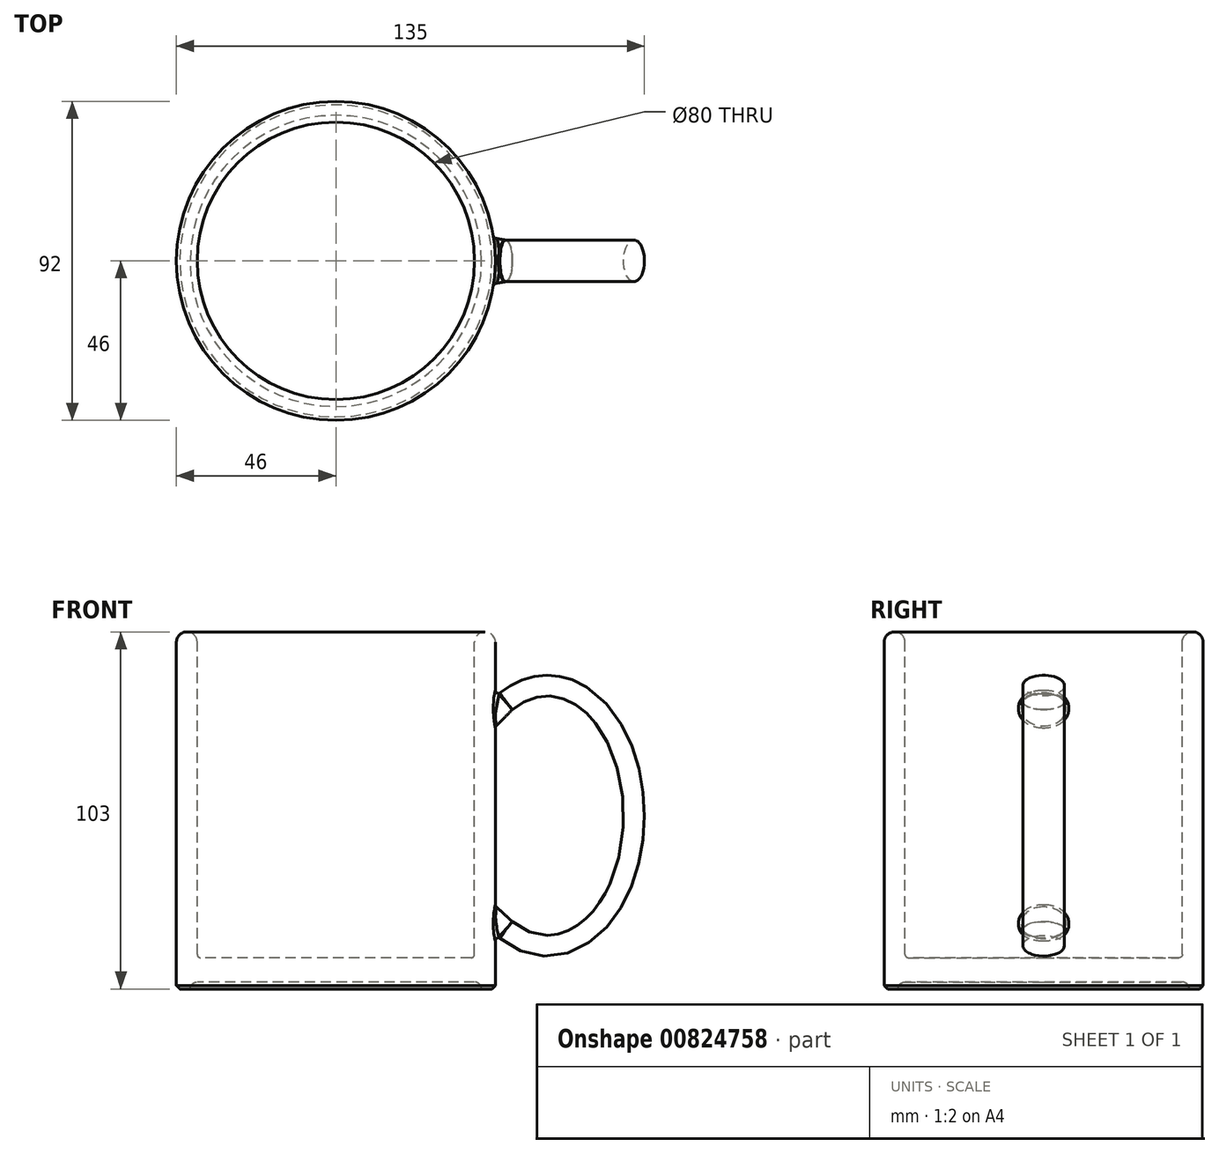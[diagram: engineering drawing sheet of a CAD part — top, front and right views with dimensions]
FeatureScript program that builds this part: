
annotation { "Feature Type Name" : "Feature", "Feature Type Description" : "" }
export const myFeature = defineFeature(function(context is Context, id is Id, definition is map)
    precondition{}
    {
        {
            var Q0;
            Q0=qCreatedBy(makeId("Front.planeOp"),FACE);
            var sketch = newSketch(context, id + "F0", { "sketchPlane" : qUnion([Q0])});
            skLineSegment(sketch, "E0", {"start": v(0, 1) * mm, "end": v(0, 91) * mm});
            skLineSegment(sketch, "E1", {"start": v(6, 91) * mm, "end": v(6, -9) * mm});
            skLineSegment(sketch, "E2", {"start": v(6, -9) * mm, "end": v(2, -9) * mm});
            skLineSegment(sketch, "E3", {"start": v(-1, 0) * mm, "end": v(-40, 0) * mm});
            skLineSegment(sketch, "E4", {"start": v(-40, 0) * mm, "end": v(-40, -7) * mm});
            skLineSegment(sketch, "E5", {"start": v(-40, -7) * mm, "end": v(0, -7) * mm});
            skLineSegment(sketch, "E6", {"start": v(2, -9) * mm, "end": v(2, -9) * mm});
            skArc(sketch, "E7", {"start": v(0, 91) * mm, "mid": v(3, 94) * mm, "end": v(6, 91) * mm});
            skPoint(sketch, "E8.visualSharp", {"position": v(2, -7) * mm});
            skArc(sketch, "E8.filletArc", {"start": v(2, -9) * mm, "mid": v(1.41, -7.59) * mm, "end": v(0, -7) * mm});
            skPoint(sketch, "E9.visualSharp", {"position": v(0, 0) * mm});
            skArc(sketch, "E9.filletArc", {"start": v(-1, 0) * mm, "mid": v(-0.3, 0.3) * mm, "end": v(0, 1) * mm});
            skLineSegment(sketch, "E10", {"start": v(6, 41) * mm, "end": v(21, 41) * mm, "construction": true});
            skEllipticalArc(sketch, "E11", {});
            skLineSegment(sketch, "E12", {"start": v(9, 87.43) * mm, "end": v(9, -6.06) * mm, "construction": true});
            const initialGuessF0  = {"E11": [0.021, 0.041, 0, 1, 0.0375, 0.025, 2.6409379411852054, 0.5006547124045883]};
            skSetInitialGuess(sketch, initialGuessF0);
            skSolve(sketch);
        }
        {
            var Q0;
            Q0=qCreatedBy(makeId("Right.planeOp"),FACE);
            var sketch = newSketch(context, id + "F1", { "sketchPlane" : qUnion([Q0])});
            skCircle(sketch, "E13", {"center": v(0, 68) * mm, "radius": 7.5 * mm});
            skCircle(sketch, "E14.0.1.0", {"center": v(0, 13) * mm, "radius": 7.5 * mm});
            skLineSegment(sketch, "E14.direction1", {"start": v(0, 68) * mm, "end": v(25, 68) * mm, "construction": true});
            skLineSegment(sketch, "E14.direction2", {"start": v(0, 68) * mm, "end": v(0, 13) * mm, "construction": true});
            skSolve(sketch);
        }
        {
            var Q0;
            Q0=qCreatedBy(makeId("Top.planeOp"),FACE);
            var Q1;
            Q1=sQuery(id+"F0.wireOp",VERTEX,"E10.end");
            cPlane(context, id + "F2", {"entities" : qUnion([Q0, Q1]), "cplaneType" : CPlaneType.PLANE_POINT, "offset" : 25 * mm, "width" : 150 * mm, "height" : 150 * mm});
        }
        {
            var Q0;
            Q0=qCreatedBy(id+"F2.planeOp",FACE);
            var sketch = newSketch(context, id + "F3", { "sketchPlane" : qUnion([Q0])});
            skLineSegment(sketch, "E15.0", {"start": v(9, 0) * mm, "end": v(46, 0) * mm, "construction": true});
            skEllipse(sketch, "E16", {"center": v(46, 0) * mm, "majorRadius": 6 * mm, "minorRadius": 3 * mm, "majorAxis": v(0, 1)});
            skSolve(sketch);
        }
        {
            var Q0;
            Q0=makeQuery(id+"F3.imprint","IMPRINT",FACE,{"disambiguationData":[TD([[makeQuery(id+"F3.imprint","IMPRINT",EDGE,{"derivedFrom":sQuery(id+"F3.wireOp",EDGE,"E16")}),1.0]])]});
            var Q1;
            Q1=sQuery(id+"F0.wireOp",EDGE,"E11");
            sweep(context, id + "F4", {"profiles" : qUnion([Q0]), "path" : qUnion([Q1])});
        }
        {
            var Q0;
            Q0=makeQuery(id+"F0.imprint","IMPRINT",FACE,{"disambiguationData":[TD([[makeQuery(id+"F0.imprint","IMPRINT",EDGE,{"derivedFrom":sQuery(id+"F0.wireOp",EDGE,"E0")}),-1.0]])]});
            var Q1;
            Q1=sQuery(id+"F0.wireOp",EDGE,"E4");
            revolve(context, id + "F5", {"operationType" : NewBodyOperationType.ADD, "surfaceOperationType" : NewSurfaceOperationType.NEW, "entities" : qUnion([Q0]), "axis" : qUnion([Q1]), "revolveType" : RevolveType.FULL});
        }
        {
            var Q0;
            Q0=makeQuery(id+"F1.imprint","IMPRINT",FACE,{"disambiguationData":[TD([[makeQuery(id+"F1.imprint","IMPRINT",EDGE,{"derivedFrom":sQuery(id+"F1.wireOp",EDGE,"E13")}),1.0]])]});
            var Q1;
            Q1=makeQuery(id+"F4.opSweep","CAP_FACE",FACE,{"disambiguationData":[OSD([sQuery(id+"F0.wireOp",VERTEX,"E11.end"),sQuery(id+"F3.wireOp",EDGE,"E16")])],"isStart":false});
            loft(context, id + "F6", {"operationType" : NewBodyOperationType.ADD, "sheetProfilesArray" : [{ "sheetProfileEntities" : qUnion([Q0]) }, { "sheetProfileEntities" : qUnion([Q1]) }]});
        }
        {
            var Q0;
            Q0=makeQuery(id+"F1.imprint","IMPRINT",FACE,{"disambiguationData":[TD([[makeQuery(id+"F1.imprint","IMPRINT",EDGE,{"derivedFrom":sQuery(id+"F1.wireOp",EDGE,"E14.0.1.0")}),1.0]])]});
            var Q1;
            Q1=makeQuery(id+"F4.opSweep","CAP_FACE",FACE,{"disambiguationData":[OSD([sQuery(id+"F0.wireOp",VERTEX,"E11.start"),sQuery(id+"F3.wireOp",EDGE,"E16")])],"isStart":true});
            loft(context, id + "F7", {"operationType" : NewBodyOperationType.ADD, "sheetProfilesArray" : [{ "sheetProfileEntities" : qUnion([Q0]) }, { "sheetProfileEntities" : qUnion([Q1]) }]});
        }
        {
            var Q0;
            Q0=makeQuery(id+"F5.opRevolve","SWEPT_EDGE",EDGE,{"disambiguationData":[OSD([sQuery(id+"F0.wireOp",EDGE,"E1"),sQuery(id+"F0.wireOp",EDGE,"E2")])]});
            chamfer(context, id + "F8", {"entities" : qUnion([Q0]), "width" : 1 * mm, "tangentPropagation" : true});
        }
        {
            var Q0;
            Q0=makeQuery(id+"F6.boolean.opBoolean","INTERSECT",EDGE,{"derivedFrom":[makeQuery(id+"F5.opRevolve","SWEPT_FACE",FACE,{"disambiguationData":[OSD([sQuery(id+"F0.wireOp",EDGE,"E1")])]}),makeQuery(id+"F6.opLoft","SWEPT_FACE",FACE,{"disambiguationData":[OSD([sQuery(id+"F0.wireOp",VERTEX,"E11.end"),sQuery(id+"F1.wireOp",EDGE,"E13"),sQuery(id+"F3.wireOp",EDGE,"E16")])]})]});
            var Q1;
            {var subQ0=sQuery(id+"F3.wireOp",EDGE,"E16");var subQ1=sQuery(id+"F0.wireOp",VERTEX,"E11.end");Q1=makeQuery(id+"F6.boolean.opBoolean","MERGE",EDGE,{"derivedFrom":[makeQuery(id+"F4.opSweep","CAP_EDGE",EDGE,{"disambiguationData":[OSD([subQ1,subQ0])],"isStart":false}),makeQuery(id+"F6.opLoft","MID_CAP_EDGE",EDGE,{"disambiguationData":[OSD([subQ1,subQ0])],"capPos":1.0})]});}
            var Q2;
            {var subQ0=sQuery(id+"F3.wireOp",EDGE,"E16");var subQ1=sQuery(id+"F0.wireOp",VERTEX,"E11.start");Q2=makeQuery(id+"F7.boolean.opBoolean","MERGE",EDGE,{"derivedFrom":[makeQuery(id+"F4.opSweep","CAP_EDGE",EDGE,{"disambiguationData":[OSD([subQ1,subQ0])],"isStart":true}),makeQuery(id+"F7.opLoft","MID_CAP_EDGE",EDGE,{"disambiguationData":[OSD([subQ1,subQ0])],"capPos":1.0})]});}
            var Q3;
            Q3=makeQuery(id+"F7.boolean.opBoolean","INTERSECT",EDGE,{"derivedFrom":[makeQuery(id+"F5.opRevolve","SWEPT_FACE",FACE,{"disambiguationData":[OSD([sQuery(id+"F0.wireOp",EDGE,"E1")])]}),makeQuery(id+"F7.opLoft","SWEPT_FACE",FACE,{"disambiguationData":[OSD([sQuery(id+"F0.wireOp",VERTEX,"E11.start"),sQuery(id+"F1.wireOp",EDGE,"E14.0.1.0"),sQuery(id+"F3.wireOp",EDGE,"E16")])]})]});
            fillet(context, id + "F9", {"entities" : qUnion([Q0, Q1, Q2, Q3]), "radius" : 1 * mm, "tangentPropagation" : true, "allowEdgeOverflow" : false});
        }
    });
